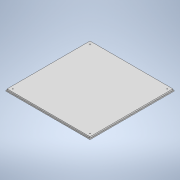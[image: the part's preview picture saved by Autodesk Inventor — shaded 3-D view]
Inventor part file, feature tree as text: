
AUTODESK INVENTOR PART (.ipt)
format: ipt  version: 2021 (Build 250183000, 183)  size: 127,488 bytes
history: native  units: mm
features: sketch x5, extrude x2, other x1, hole x1
ambient origin geometry x8: Origin, YZ Plane, XZ Plane, XY Plane, X Axis, Y Axis, Z Axis, Center Point
bodies: Body1 (feature_tree)
feature tree (9):
  other  "Sólido1"
  extrude  "Extrusión1"  Depth=206.0mm
  hole  "Agujero1"  [1 undecoded]
  extrude  "Extrusión3"  Depth=203.0mm
  sketch  "Boceto5"  dims[d17=2.0mm d18=6.0mm d19=4.0mm d20=2.0mm d21=90.0deg d22=25.0mm d23=20.594885mm d24=203.0mm]
  sketch  "Boceto6"  dims[d25=203.0mm d26=206.0mm d27=206.0mm d28=3.0mm d29=0.0mm]
  sketch  "Boceto1"  dims[d0=206.0mm d1=206.0mm]
  sketch  "Boceto3"  dims[d2=5.0mm d3=0.0mm d12=2.0mm]
  sketch  "Boceto4"  dims[d13=40.0mm d15=360.0deg]
note: 1 required parameter value undecoded (feature->parameter linkage not recoverable at this tier; creation-order binding heuristic only, values carry confidence <= 0.55)
